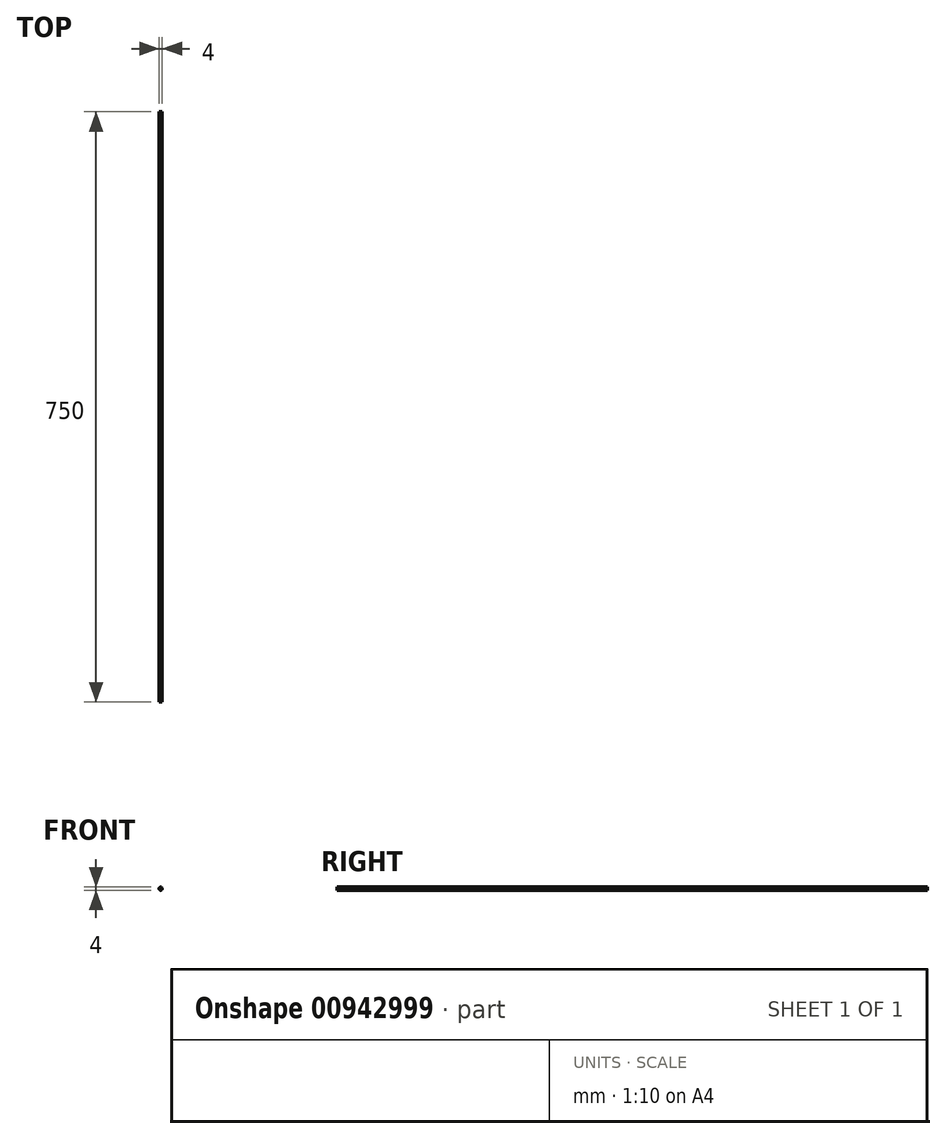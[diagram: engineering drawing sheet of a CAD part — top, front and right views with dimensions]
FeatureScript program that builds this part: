
annotation { "Feature Type Name" : "Feature", "Feature Type Description" : "" }
export const myFeature = defineFeature(function(context is Context, id is Id, definition is map)
    precondition{}
    {
        {
            var Q0;
            Q0=qCreatedBy(makeId("Front.planeOp"),FACE);
            var sketch = newSketch(context, id + "F0", { "sketchPlane" : qUnion([Q0])});
            skCircle(sketch, "E0", {"center": v(-38.68, 0.9) * mm, "radius": 2 * mm});
            skSolve(sketch);
        }
        {
            var Q0;
            Q0 = qSketchRegion(id + "F0", true);
            extrude(context, id + "F1", {"entities" : qUnion([Q0]), "depth" : 750 * mm, "offsetDistance" : 25 * mm});
        }
    });
